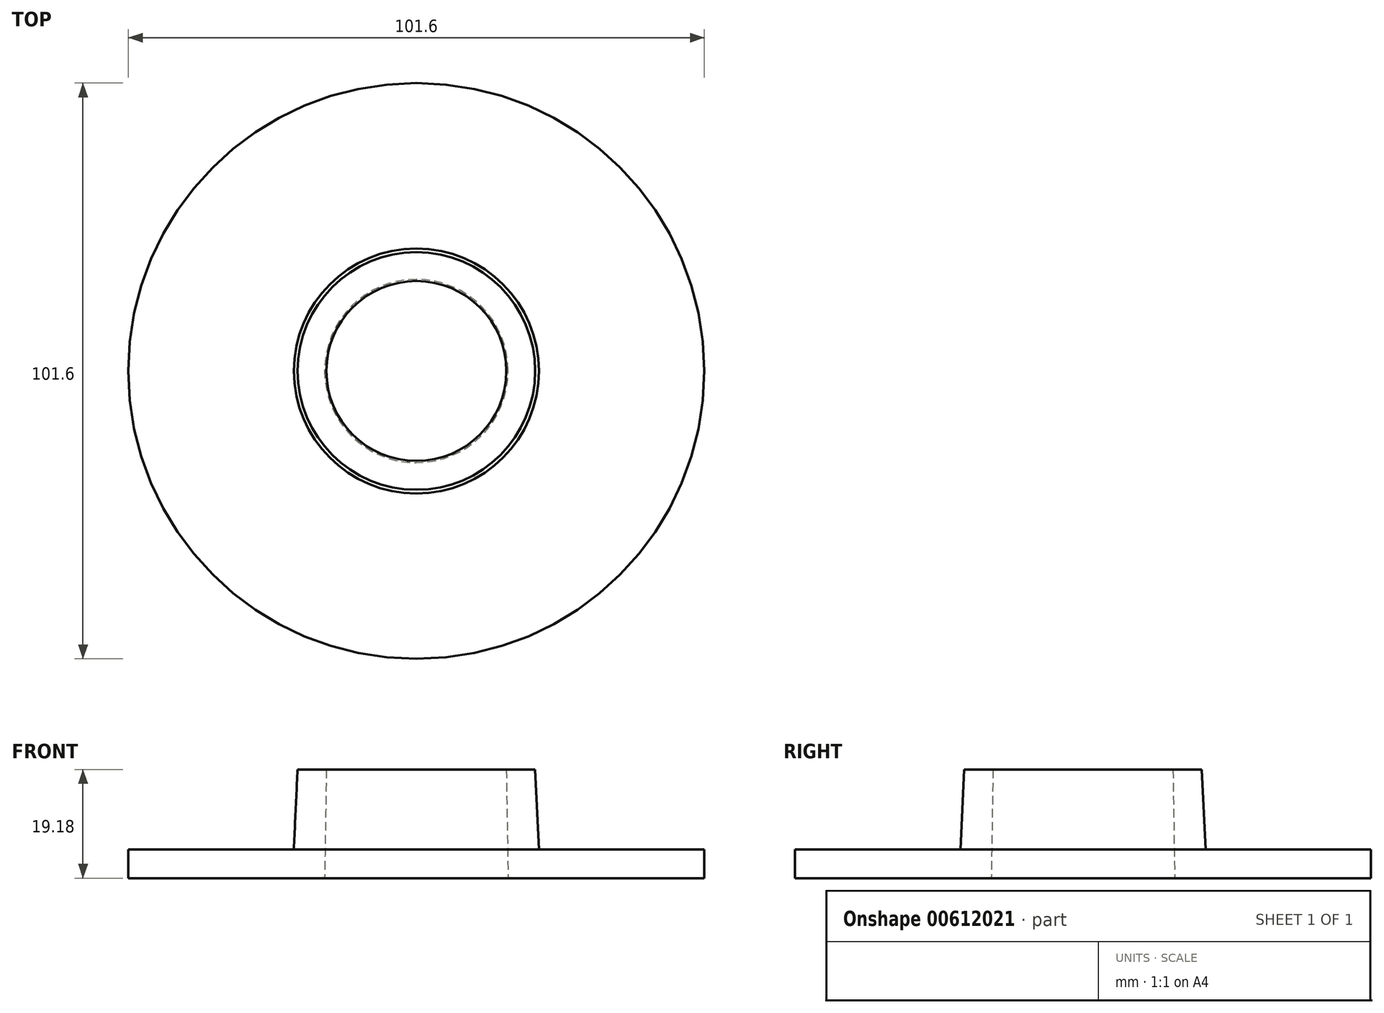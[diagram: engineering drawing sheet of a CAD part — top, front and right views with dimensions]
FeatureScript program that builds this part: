
annotation { "Feature Type Name" : "Feature", "Feature Type Description" : "" }
export const myFeature = defineFeature(function(context is Context, id is Id, definition is map)
    precondition{}
    {
        {
            var Q0;
            Q0=qCreatedBy(makeId("Front.planeOp"),FACE);
            var sketch = newSketch(context, id + "F0", { "sketchPlane" : qUnion([Q0])});
            skLineSegment(sketch, "E0", {"start": v(0, 0) * mm, "end": v(0, 19.1) * mm, "construction": true});
            skLineSegment(sketch, "E1", {"start": v(0, 19.1) * mm, "end": v(-15.88, 19.1) * mm, "construction": true});
            skLineSegment(sketch, "E2", {"start": v(0, 0) * mm, "end": v(-16.18, 0) * mm, "construction": true});
            skLineSegment(sketch, "E3", {"start": v(-16.18, 0) * mm, "end": v(-50.8, 0) * mm});
            skLineSegment(sketch, "E4", {"start": v(-50.8, 0) * mm, "end": v(-50.8, 5.08) * mm});
            skLineSegment(sketch, "E5", {"start": v(-50.8, 5.08) * mm, "end": v(-21.62, 5.08) * mm});
            skLineSegment(sketch, "E6", {"start": v(-16.18, 0) * mm, "end": v(-15.88, 19.1) * mm});
            skLineSegment(sketch, "E7", {"start": v(-15.88, 19.1) * mm, "end": v(-20.95, 19.18) * mm});
            skLineSegment(sketch, "E8", {"start": v(-20.95, 19.18) * mm, "end": v(-21.62, 5.08) * mm});
            skSolve(sketch);
        }
        {
            var Q0;
            Q0=makeQuery(id+"F0.imprint","IMPRINT",FACE,{"disambiguationData":[TD([[makeQuery(id+"F0.imprint","IMPRINT",EDGE,{"derivedFrom":sQuery(id+"F0.wireOp",EDGE,"E3")}),-1.0]])]});
            var Q1;
            Q1=sQuery(id+"F0.wireOp",EDGE,"E0");
            revolve(context, id + "F1", {"entities" : qUnion([Q0]), "axis" : qUnion([Q1]), "revolveType" : RevolveType.FULL});
        }
    });
